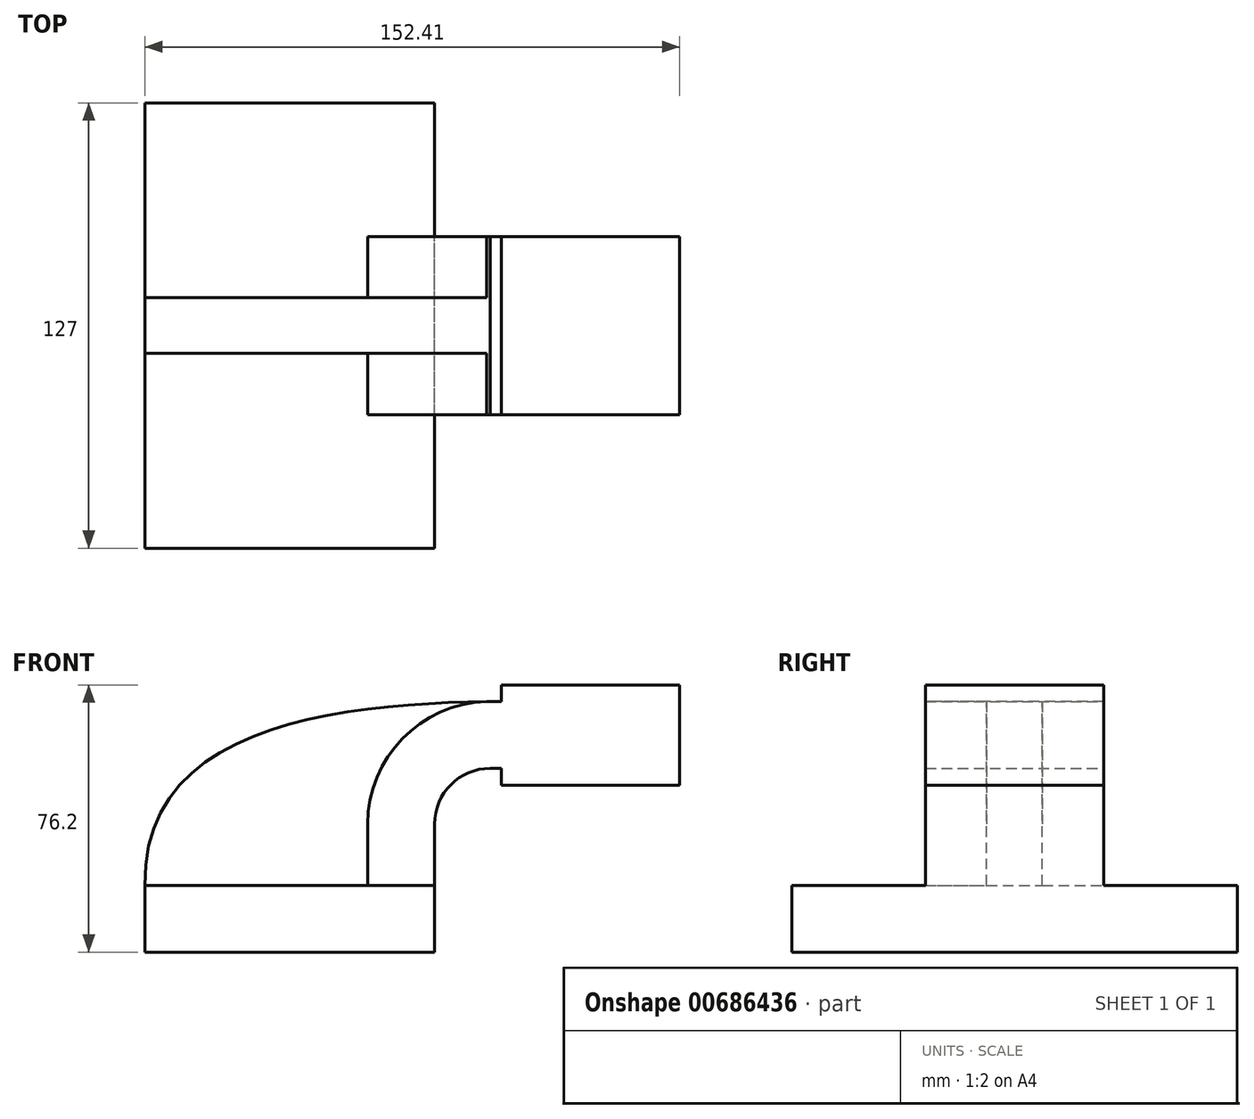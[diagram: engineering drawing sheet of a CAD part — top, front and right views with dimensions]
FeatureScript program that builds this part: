
annotation { "Feature Type Name" : "Feature", "Feature Type Description" : "" }
export const myFeature = defineFeature(function(context is Context, id is Id, definition is map)
    precondition{}
    {
        {
            var Q0;
            Q0=qCreatedBy(makeId("Front.planeOp"),FACE);
            var sketch = newSketch(context, id + "F0", { "sketchPlane" : qUnion([Q0])});
            skLineSegment(sketch, "E0.bottom", {"start": v(-41.28, -9.53) * mm, "end": v(41.28, -9.53) * mm});
            skLineSegment(sketch, "E0.top", {"start": v(-41.28, 9.52) * mm, "end": v(41.27, 9.52) * mm});
            skLineSegment(sketch, "E0.left", {"start": v(-41.27, -9.53) * mm, "end": v(-41.28, 9.52) * mm});
            skLineSegment(sketch, "E0.right", {"start": v(41.28, -9.53) * mm, "end": v(41.27, 9.52) * mm});
            skPoint(sketch, "E0.middle", {"position": v(0, 0) * mm});
            skLineSegment(sketch, "E1.bottom", {"start": v(60.32, 38.1) * mm, "end": v(111.12, 38.1) * mm});
            skLineSegment(sketch, "E1.top", {"start": v(60.32, 66.67) * mm, "end": v(111.12, 66.67) * mm});
            skLineSegment(sketch, "E1.left", {"start": v(60.32, 38.1) * mm, "end": v(60.32, 66.67) * mm});
            skLineSegment(sketch, "E1.right", {"start": v(111.12, 38.1) * mm, "end": v(111.12, 66.67) * mm});
            skPoint(sketch, "E1.middle", {"position": v(85.72, 52.39) * mm});
            skLineSegment(sketch, "E2", {"start": v(41.27, 9.52) * mm, "end": v(41.27, 27) * mm});
            skArc(sketch, "E3", {"start": v(41.27, 27) * mm, "mid": v(45.92, 38.23) * mm, "end": v(57.15, 42.88) * mm});
            skLineSegment(sketch, "E4", {"start": v(57.15, 42.88) * mm, "end": v(88.61, 42.88) * mm});
            skLineSegment(sketch, "E5.0", {"start": v(57.15, 61.93) * mm, "end": v(88.4, 61.93) * mm});
            skArc(sketch, "E5.1", {"start": v(22.22, 27) * mm, "mid": v(32.45, 51.7) * mm, "end": v(57.15, 61.93) * mm});
            skLineSegment(sketch, "E5.2", {"start": v(22.22, 9.52) * mm, "end": v(22.22, 27) * mm});
            skLineSegment(sketch, "E6", {"start": v(88.92, 38.1) * mm, "end": v(88.4, 66.67) * mm});
            skFitSpline(sketch, "E7", {"points": [v(-41.28, 9.53) * mm, v(57.15, 61.93) * mm], "startDerivative": vector(-2.73, 140.53) * mm, "endDerivative": vector(121.42, 1.72) * mm});
            skSolve(sketch);
        }
        {
            var Q0;
            Q0=makeQuery(id+"F0.imprint","IMPRINT",FACE,{"disambiguationData":[TD([[makeQuery(id+"F0.imprint","IMPRINT",EDGE,{"derivedFrom":sQuery(id+"F0.wireOp",EDGE,"E0.bottom")}),1.0]])]});
            extrude(context, id + "F1", {"entities" : qUnion([Q0]), "endBound" : BoundingType.SYMMETRIC, "depth" : 127 * mm, "offsetDistance" : 25.4 * mm});
        }
        {
            var Q0;
            {var subQ1=sQuery(id+"F0.wireOp",EDGE,"E2");Q0=makeQuery(id+"F0.imprint","IMPRINT",FACE,{"disambiguationData":[TD([[makeQuery(id+"F0.imprint","IMPRINT",EDGE,{"derivedFrom":subQ1}),1.0]])]});}
            var Q1;
            {var subQ0=sQuery(id+"F0.wireOp",EDGE,"E1.right");Q1=makeQuery(id+"F0.imprint","IMPRINT",FACE,{"disambiguationData":[TD([[makeQuery(id+"F0.imprint","IMPRINT",EDGE,{"derivedFrom":subQ0}),1.0]])]});}
            var Q2;
            {var subQ4=sQuery(id+"F0.wireOp",EDGE,"E6");Q2=makeQuery(id+"F0.imprint","IMPRINT",FACE,{"disambiguationData":[TD([[makeQuery(id+"F0.imprint","IMPRINT",EDGE,{"derivedFrom":subQ4}),1.0]])]});}
            extrude(context, id + "F2", {"entities" : qUnion([Q0, Q1, Q2]), "operationType" : NewBodyOperationType.ADD, "endBound" : BoundingType.SYMMETRIC, "depth" : 50.8 * mm, "offsetDistance" : 25.4 * mm});
        }
        {
            var Q0;
            {var subQ3=sQuery(id+"F0.wireOp",EDGE,"E5.2");Q0=makeQuery(id+"F0.imprint","IMPRINT",FACE,{"disambiguationData":[TD([[makeQuery(id+"F0.imprint","IMPRINT",EDGE,{"derivedFrom":subQ3}),1.0]])]});}
            extrude(context, id + "F3", {"entities" : qUnion([Q0]), "operationType" : NewBodyOperationType.ADD, "endBound" : BoundingType.SYMMETRIC, "depth" : 15.88 * mm, "offsetDistance" : 25.4 * mm});
        }
    });
